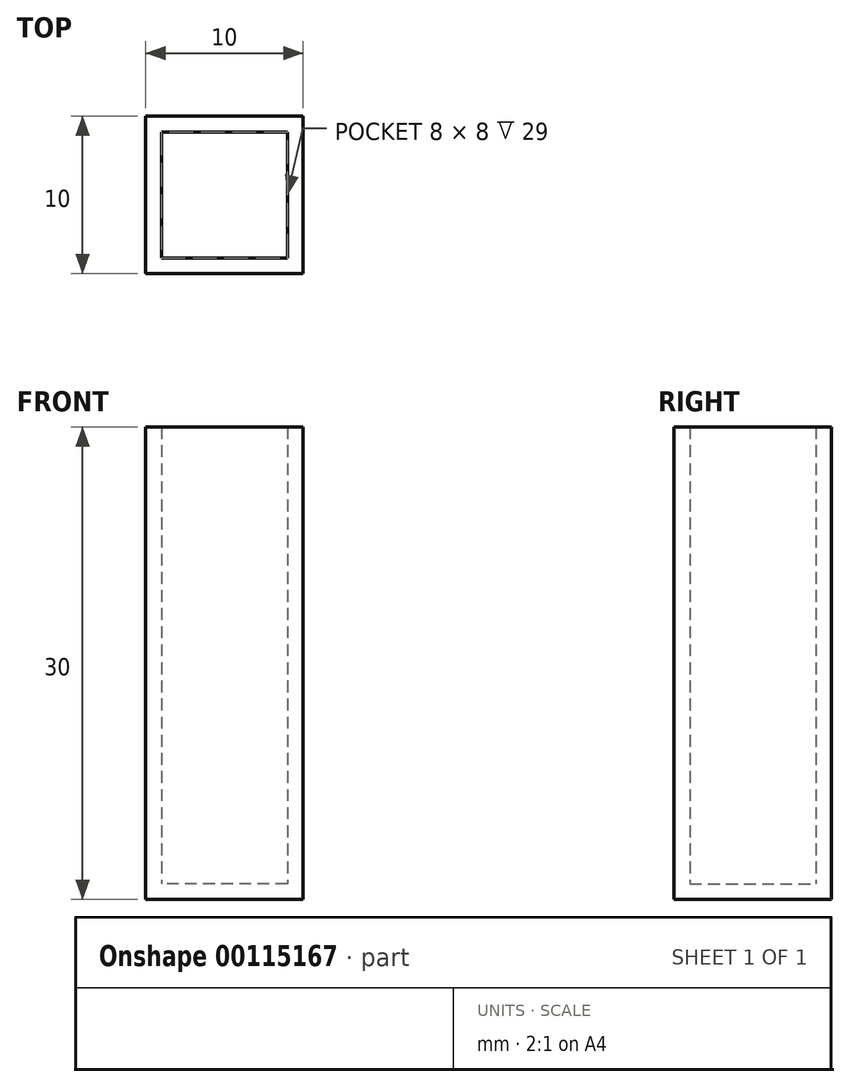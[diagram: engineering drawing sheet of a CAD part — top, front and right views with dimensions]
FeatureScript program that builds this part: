
annotation { "Feature Type Name" : "Feature", "Feature Type Description" : "" }
export const myFeature = defineFeature(function(context is Context, id is Id, definition is map)
    precondition{}
    {
        {
            var Q0;
            Q0=qCreatedBy(makeId("Top.planeOp"),FACE);
            var sketch = newSketch(context, id + "F0", { "sketchPlane" : qUnion([Q0])});
            skLineSegment(sketch, "E0.bottom", {"start": v(5, -5) * mm, "end": v(-5, -5) * mm});
            skLineSegment(sketch, "E0.top", {"start": v(5, 5) * mm, "end": v(-5, 5) * mm});
            skLineSegment(sketch, "E0.left", {"start": v(5, -5) * mm, "end": v(5, 5) * mm});
            skLineSegment(sketch, "E0.right", {"start": v(-5, -5) * mm, "end": v(-5, 5) * mm});
            skPoint(sketch, "E0.middle", {"position": v(0, 0) * mm});
            skLineSegment(sketch, "E1.0", {"start": v(4, 4) * mm, "end": v(-4, 4) * mm});
            skLineSegment(sketch, "E1.1", {"start": v(4, -4) * mm, "end": v(4, 4) * mm});
            skLineSegment(sketch, "E1.2", {"start": v(4, -4) * mm, "end": v(-4, -4) * mm});
            skLineSegment(sketch, "E1.3", {"start": v(-4, -4) * mm, "end": v(-4, 4) * mm});
            skSolve(sketch);
        }
        {
            var Q0;
            Q0=makeQuery(id+"F0.imprint","IMPRINT",FACE,{"disambiguationData":[TD([[makeQuery(id+"F0.imprint","IMPRINT",EDGE,{"derivedFrom":sQuery(id+"F0.wireOp",EDGE,"E1.0")}),1.0]])]});
            extrude(context, id + "F1", {"entities" : qUnion([Q0]), "depth" : 1 * mm});
        }
        {
            var Q0;
            Q0=makeQuery(id+"F0.imprint","IMPRINT",FACE,{"disambiguationData":[TD([[makeQuery(id+"F0.imprint","IMPRINT",EDGE,{"derivedFrom":sQuery(id+"F0.wireOp",EDGE,"E0.bottom")}),-1.0]])]});
            extrude(context, id + "F2", {"entities" : qUnion([Q0]), "operationType" : NewBodyOperationType.ADD, "depth" : 30 * mm});
        }
    });
